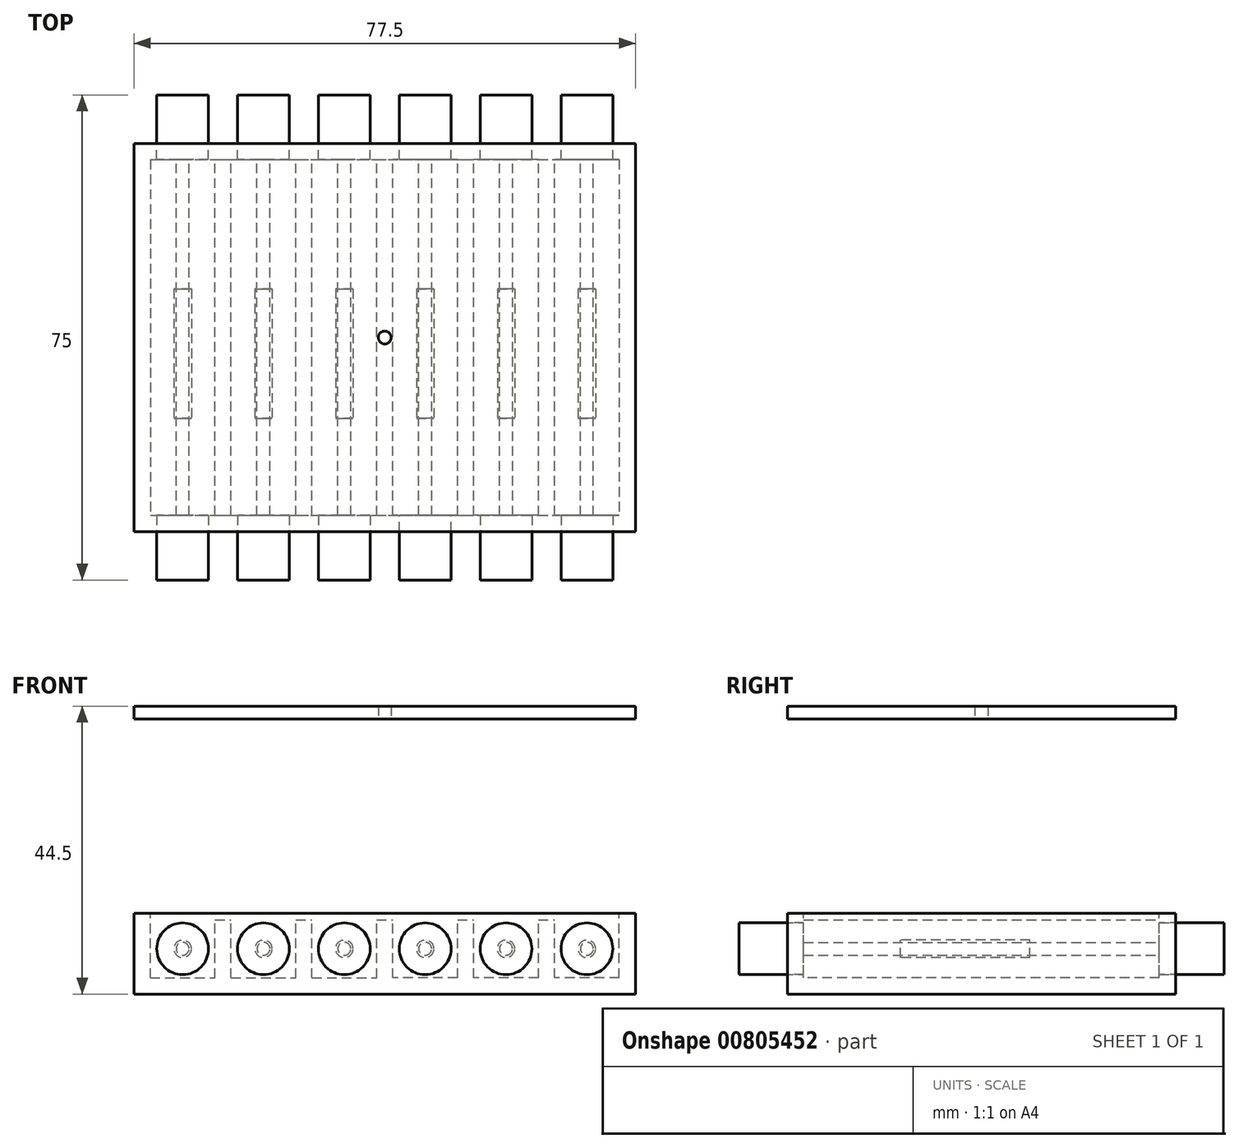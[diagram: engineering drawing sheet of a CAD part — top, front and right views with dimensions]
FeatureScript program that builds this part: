
annotation { "Feature Type Name" : "Feature", "Feature Type Description" : "" }
export const myFeature = defineFeature(function(context is Context, id is Id, definition is map)
    precondition{}
    {
        {
            var Q0;
            Q0=qCreatedBy(makeId("Top.planeOp"),FACE);
            var sketch = newSketch(context, id + "F0", { "sketchPlane" : qUnion([Q0])});
            skLineSegment(sketch, "E0.bottom", {"start": v(38.75, -30) * mm, "end": v(-38.75, -30) * mm});
            skLineSegment(sketch, "E0.top", {"start": v(38.75, 30) * mm, "end": v(-38.75, 30) * mm});
            skLineSegment(sketch, "E0.left", {"start": v(38.75, -30) * mm, "end": v(38.75, 30) * mm});
            skLineSegment(sketch, "E0.right", {"start": v(-38.75, -30) * mm, "end": v(-38.75, 30) * mm});
            skPoint(sketch, "E0.middle", {"position": v(0, 0) * mm});
            skSolve(sketch);
        }
        {
            var Q0;
            Q0 = qSketchRegion(id + "F0", true);
            extrude(context, id + "F1", {"entities" : qUnion([Q0]), "depth" : 12.5 * mm, "offsetDistance" : 25 * mm});
        }
        {
            var Q0;
            Q0=makeQuery(id+"F1.opExtrude","CAP_FACE",FACE,{"disambiguationData":[OSD([sQuery(id+"F0.wireOp",EDGE,"E0.bottom"),sQuery(id+"F0.wireOp",EDGE,"E0.top"),sQuery(id+"F0.wireOp",EDGE,"E0.left"),sQuery(id+"F0.wireOp",EDGE,"E0.right")])],"isStart":false});
            var sketch = newSketch(context, id + "F2", { "sketchPlane" : qUnion([Q0])});
            skLineSegment(sketch, "E1.bottom", {"start": v(-36.25, 27.5) * mm, "end": v(-26.25, 27.5) * mm});
            skLineSegment(sketch, "E1.top", {"start": v(-36.25, -27.5) * mm, "end": v(-26.25, -27.5) * mm});
            skLineSegment(sketch, "E1.left", {"start": v(-36.25, 27.5) * mm, "end": v(-36.25, -27.5) * mm});
            skLineSegment(sketch, "E1.right", {"start": v(-26.25, 27.5) * mm, "end": v(-26.25, -27.5) * mm});
            skLineSegment(sketch, "E2.MirrorCS", {"start": v(36.25, 27.5) * mm, "end": v(26.25, 27.5) * mm});
            skLineSegment(sketch, "E3.MirrorCS", {"start": v(36.25, 27.5) * mm, "end": v(36.25, -27.5) * mm});
            skLineSegment(sketch, "E4.MirrorCS", {"start": v(26.25, 27.5) * mm, "end": v(26.25, -27.5) * mm});
            skLineSegment(sketch, "E5.MirrorCS", {"start": v(36.25, -27.5) * mm, "end": v(26.25, -27.5) * mm});
            skLineSegment(sketch, "E6.bottom", {"start": v(-23.75, 27.5) * mm, "end": v(-13.75, 27.5) * mm});
            skLineSegment(sketch, "E6.top", {"start": v(-23.75, -27.5) * mm, "end": v(-13.75, -27.5) * mm});
            skLineSegment(sketch, "E6.left", {"start": v(-23.75, 27.5) * mm, "end": v(-23.75, -27.5) * mm});
            skLineSegment(sketch, "E6.right", {"start": v(-13.75, 27.5) * mm, "end": v(-13.75, -27.5) * mm});
            skPoint(sketch, "E7.firstSnap0", {"position": v(-18.75, 27.5) * mm});
            skLineSegment(sketch, "E7.bottom", {"start": v(-11.25, 27.5) * mm, "end": v(-1.25, 27.5) * mm});
            skLineSegment(sketch, "E7.top", {"start": v(-11.25, -27.5) * mm, "end": v(-1.25, -27.5) * mm});
            skLineSegment(sketch, "E7.left", {"start": v(-11.25, 27.5) * mm, "end": v(-11.25, -27.5) * mm});
            skLineSegment(sketch, "E7.right", {"start": v(-1.25, 27.5) * mm, "end": v(-1.25, -27.5) * mm});
            skLineSegment(sketch, "E8.MirrorCS", {"start": v(23.75, 27.5) * mm, "end": v(13.75, 27.5) * mm});
            skLineSegment(sketch, "E9.MirrorCS", {"start": v(11.25, 27.5) * mm, "end": v(1.25, 27.5) * mm});
            skLineSegment(sketch, "E10.MirrorCS", {"start": v(13.75, 27.5) * mm, "end": v(13.75, -27.5) * mm});
            skLineSegment(sketch, "E11.MirrorCS", {"start": v(11.25, 27.5) * mm, "end": v(11.25, -27.5) * mm});
            skLineSegment(sketch, "E12.MirrorCS", {"start": v(1.25, 27.5) * mm, "end": v(1.25, -27.5) * mm});
            skLineSegment(sketch, "E13.MirrorCS", {"start": v(23.75, 27.5) * mm, "end": v(23.75, -27.5) * mm});
            skLineSegment(sketch, "E14.MirrorCS", {"start": v(23.75, -27.5) * mm, "end": v(13.75, -27.5) * mm});
            skLineSegment(sketch, "E15.MirrorCS", {"start": v(11.25, -27.5) * mm, "end": v(1.25, -27.5) * mm});
            skSolve(sketch);
        }
        {
            var Q0;
            Q0 = qSketchRegion(id + "F2", true);
            extrude(context, id + "F3", {"entities" : qUnion([Q0]), "operationType" : NewBodyOperationType.REMOVE, "oppositeDirection" : true, "depth" : 10 * mm, "offsetDistance" : 25 * mm});
        }
        {
            var Q0;
            Q0=makeQuery(id+"F1.opExtrude","SWEPT_FACE",FACE,{"disambiguationData":[OSD([sQuery(id+"F0.wireOp",EDGE,"E0.bottom")])]});
            var sketch = newSketch(context, id + "F4", { "sketchPlane" : qUnion([Q0])});
            skCircle(sketch, "E16", {"center": v(-31.25, 7) * mm, "radius": 4 * mm});
            skCircle(sketch, "E17", {"center": v(-18.75, 7) * mm, "radius": 4 * mm});
            skCircle(sketch, "E18", {"center": v(-6.25, 7) * mm, "radius": 4 * mm});
            skCircle(sketch, "E19.MirrorC", {"center": v(6.25, 7) * mm, "radius": 4 * mm});
            skCircle(sketch, "E20.MirrorC", {"center": v(18.75, 7) * mm, "radius": 4 * mm});
            skCircle(sketch, "E21.MirrorC", {"center": v(31.25, 7) * mm, "radius": 4 * mm});
            skSolve(sketch);
        }
        {
            var Q0;
            Q0 = qSketchRegion(id + "F4", true);
            var Q1;
            Q1=makeQuery(id+"F3.boolean.opBoolean","COPY",FACE,{"derivedFrom":makeQuery(id+"F3.opExtrude","SWEPT_FACE",FACE,{"disambiguationData":[OSD([sQuery(id+"F2.wireOp",EDGE,"E1.top")])]})});
            extrude(context, id + "F5", {"entities" : qUnion([Q0]), "endBound" : BoundingType.UP_TO_SURFACE, "oppositeDirection" : true, "depth" : 25 * mm, "endBoundEntityFace" : qUnion([Q1]), "offsetDistance" : 25 * mm});
        }
        {
            var Q0;
            Q0=makeQuery(id+"F1.opExtrude","CAP_FACE",FACE,{"disambiguationData":[OSD([sQuery(id+"F0.wireOp",EDGE,"E0.bottom"),sQuery(id+"F0.wireOp",EDGE,"E0.top"),sQuery(id+"F0.wireOp",EDGE,"E0.left"),sQuery(id+"F0.wireOp",EDGE,"E0.right")])],"isStart":false});
            var sketch = newSketch(context, id + "F6", { "sketchPlane" : qUnion([Q0])});
            skLineSegment(sketch, "E22.bottom", {"start": v(36.25, -27.5) * mm, "end": v(-36.25, -27.5) * mm});
            skLineSegment(sketch, "E22.top", {"start": v(36.25, 27.5) * mm, "end": v(-36.25, 27.5) * mm});
            skLineSegment(sketch, "E22.left", {"start": v(36.25, -27.5) * mm, "end": v(36.25, 27.5) * mm});
            skLineSegment(sketch, "E22.right", {"start": v(-36.25, -27.5) * mm, "end": v(-36.25, 27.5) * mm});
            skPoint(sketch, "E22.middle", {"position": v(0, 0) * mm});
            skSolve(sketch);
        }
        {
            var Q0;
            Q0 = qSketchRegion(id + "F6", true);
            extrude(context, id + "F7", {"entities" : qUnion([Q0]), "operationType" : NewBodyOperationType.REMOVE, "oppositeDirection" : true, "depth" : 1 * mm, "offsetDistance" : 25 * mm});
        }
        {
            var Q0;
            Q0=makeQuery(id+"F5.opExtrude","SWEPT_BODY",BODY,{"disambiguationData":[OSD([sQuery(id+"F4.wireOp",EDGE,"E16")])]});
            var Q1;
            Q1=makeQuery(id+"F5.opExtrude","SWEPT_BODY",BODY,{"disambiguationData":[OSD([sQuery(id+"F4.wireOp",EDGE,"E17")])]});
            var Q2;
            Q2=makeQuery(id+"F5.opExtrude","SWEPT_BODY",BODY,{"disambiguationData":[OSD([sQuery(id+"F4.wireOp",EDGE,"E18")])]});
            var Q3;
            Q3=makeQuery(id+"F5.opExtrude","SWEPT_BODY",BODY,{"disambiguationData":[OSD([sQuery(id+"F4.wireOp",EDGE,"E20.MirrorC")])]});
            var Q4;
            Q4=makeQuery(id+"F5.opExtrude","SWEPT_BODY",BODY,{"disambiguationData":[OSD([sQuery(id+"F4.wireOp",EDGE,"E21.MirrorC")])]});
            var Q5;
            Q5=makeQuery(id+"F5.opExtrude","SWEPT_BODY",BODY,{"disambiguationData":[OSD([sQuery(id+"F4.wireOp",EDGE,"E19.MirrorC")])]});
            var Q6;
            Q6=qCreatedBy(makeId("Front.planeOp"),FACE);
            mirror(context, id + "F8", {"entities" : qUnion([Q0, Q1, Q2, Q3, Q4, Q5]), "mirrorPlane" : qUnion([Q6])});
        }
        {
            var Q0;
            Q0=makeQuery(id+"F5.opExtrude","SWEPT_BODY",BODY,{"disambiguationData":[OSD([sQuery(id+"F4.wireOp",EDGE,"E16")])]});
            var Q1;
            Q1=makeQuery(id+"F8.opPattern","COPY",BODY,{"derivedFrom":makeQuery(id+"F5.opExtrude","SWEPT_BODY",BODY,{"disambiguationData":[OSD([sQuery(id+"F4.wireOp",EDGE,"E16")])]}),"instanceName":"1"});
            var Q2;
            Q2=makeQuery(id+"F5.opExtrude","SWEPT_BODY",BODY,{"disambiguationData":[OSD([sQuery(id+"F4.wireOp",EDGE,"E17")])]});
            var Q3;
            Q3=makeQuery(id+"F5.opExtrude","SWEPT_BODY",BODY,{"disambiguationData":[OSD([sQuery(id+"F4.wireOp",EDGE,"E18")])]});
            var Q4;
            Q4=makeQuery(id+"F5.opExtrude","SWEPT_BODY",BODY,{"disambiguationData":[OSD([sQuery(id+"F4.wireOp",EDGE,"E19.MirrorC")])]});
            var Q5;
            Q5=makeQuery(id+"F5.opExtrude","SWEPT_BODY",BODY,{"disambiguationData":[OSD([sQuery(id+"F4.wireOp",EDGE,"E20.MirrorC")])]});
            var Q6;
            Q6=makeQuery(id+"F5.opExtrude","SWEPT_BODY",BODY,{"disambiguationData":[OSD([sQuery(id+"F4.wireOp",EDGE,"E21.MirrorC")])]});
            var Q7;
            Q7=makeQuery(id+"F8.opPattern","COPY",BODY,{"derivedFrom":makeQuery(id+"F5.opExtrude","SWEPT_BODY",BODY,{"disambiguationData":[OSD([sQuery(id+"F4.wireOp",EDGE,"E17")])]}),"instanceName":"1"});
            var Q8;
            Q8=makeQuery(id+"F8.opPattern","COPY",BODY,{"derivedFrom":makeQuery(id+"F5.opExtrude","SWEPT_BODY",BODY,{"disambiguationData":[OSD([sQuery(id+"F4.wireOp",EDGE,"E18")])]}),"instanceName":"1"});
            var Q9;
            Q9=makeQuery(id+"F8.opPattern","COPY",BODY,{"derivedFrom":makeQuery(id+"F5.opExtrude","SWEPT_BODY",BODY,{"disambiguationData":[OSD([sQuery(id+"F4.wireOp",EDGE,"E19.MirrorC")])]}),"instanceName":"1"});
            var Q10;
            Q10=makeQuery(id+"F8.opPattern","COPY",BODY,{"derivedFrom":makeQuery(id+"F5.opExtrude","SWEPT_BODY",BODY,{"disambiguationData":[OSD([sQuery(id+"F4.wireOp",EDGE,"E20.MirrorC")])]}),"instanceName":"1"});
            var Q11;
            Q11=makeQuery(id+"F8.opPattern","COPY",BODY,{"derivedFrom":makeQuery(id+"F5.opExtrude","SWEPT_BODY",BODY,{"disambiguationData":[OSD([sQuery(id+"F4.wireOp",EDGE,"E21.MirrorC")])]}),"instanceName":"1"});
            var Q12;
            Q12=makeQuery(id+"F1.opExtrude","SWEPT_BODY",BODY,{"disambiguationData":[OSD([sQuery(id+"F0.wireOp",EDGE,"E0.bottom"),sQuery(id+"F0.wireOp",EDGE,"E0.top"),sQuery(id+"F0.wireOp",EDGE,"E0.left"),sQuery(id+"F0.wireOp",EDGE,"E0.right")])]});
            booleanBodies(context, id + "F9", {"operationType" : BooleanOperationType.SUBTRACTION, "tools" : qUnion([Q0, Q1, Q2, Q3, Q4, Q5, Q6, Q7, Q8, Q9, Q10, Q11]), "targets" : qUnion([Q12])});
        }
        {
            var Q0;
            Q0=makeQuery(id+"F1.opExtrude","CAP_FACE",FACE,{"disambiguationData":[OSD([sQuery(id+"F0.wireOp",EDGE,"E0.bottom"),sQuery(id+"F0.wireOp",EDGE,"E0.top"),sQuery(id+"F0.wireOp",EDGE,"E0.left"),sQuery(id+"F0.wireOp",EDGE,"E0.right")])],"isStart":false});
            var sketch = newSketch(context, id + "F10", { "sketchPlane" : qUnion([Q0])});
            skLineSegment(sketch, "E23.bottom", {"start": v(-38.75, 30) * mm, "end": v(38.75, 30) * mm});
            skLineSegment(sketch, "E23.top", {"start": v(-38.75, -30) * mm, "end": v(38.75, -30) * mm});
            skLineSegment(sketch, "E23.left", {"start": v(-38.75, 30) * mm, "end": v(-38.75, -30) * mm});
            skLineSegment(sketch, "E23.right", {"start": v(38.75, 30) * mm, "end": v(38.75, -30) * mm});
            skPoint(sketch, "E23.middle", {"position": v(0, 0) * mm});
            skSolve(sketch);
        }
        {
            var Q0;
            Q0 = qSketchRegion(id + "F10", true);
            extrude(context, id + "F11", {"entities" : qUnion([Q0]), "depth" : 2 * mm, "offsetDistance" : 25 * mm});
        }
        {
            var Q0;
            Q0=makeQuery(id+"F11.opExtrude","SWEPT_BODY",BODY,{"disambiguationData":[OSD([sQuery(id+"F10.wireOp",EDGE,"E23.bottom"),sQuery(id+"F10.wireOp",EDGE,"E23.top"),sQuery(id+"F10.wireOp",EDGE,"E23.left"),sQuery(id+"F10.wireOp",EDGE,"E23.right")])]});
            transform(context, id + "F12", {"entities" : qUnion([Q0]), "transformType" : TransformType.TRANSLATION_3D, "dx" : 0 * mm, "dy" : 0 * mm, "dz" : 30 * mm, "makeCopy" : false});
        }
        {
            var Q0;
            Q0=sQuery(id+"F10.wireOp",VERTEX,"E23.middle");
            var Q1;
            Q1=makeQuery(id+"F11.opExtrude","SWEPT_BODY",BODY,{"disambiguationData":[OSD([sQuery(id+"F10.wireOp",EDGE,"E23.bottom"),sQuery(id+"F10.wireOp",EDGE,"E23.top"),sQuery(id+"F10.wireOp",EDGE,"E23.left"),sQuery(id+"F10.wireOp",EDGE,"E23.right")])]});
            hole(context, id + "F13", {"style" : HoleStyle.SIMPLE, "endStyle" : HoleEndStyle.THROUGH, "oppositeDirection" : true, "standardTappedOrClearance" : lookupTablePath({ "standard" : "ANSI", "engagement" : "75%", "pitch" : "48 tpi", "size" : "#3", "type" : "Tapped" }), "standardBlindInLast" : lookupTablePath({ "standard" : "ANSI", "engagement" : "75%", "pitch" : "48 tpi", "size" : "#3", "type" : "Tapped" }), "holeDiameter" : 2 * mm, "majorDiameter" : 2.5 * mm, "showTappedDepth" : true, "isTappedThrough" : true, "tappedDepth" : 12 * mm, "tapClearance" : 3, "locations" : qUnion([Q0]), "scope" : qUnion([Q1])});
        }
        {
            var Q0;
            Q0=makeQuery(id+"F7.boolean.opBoolean","MERGE",FACE,{"derivedFrom":[makeQuery(id+"F3.boolean.opBoolean","COPY",FACE,{"derivedFrom":makeQuery(id+"F3.opExtrude","SWEPT_FACE",FACE,{"disambiguationData":[OSD([sQuery(id+"F2.wireOp",EDGE,"E1.bottom")])]})}),makeQuery(id+"F3.boolean.opBoolean","COPY",FACE,{"derivedFrom":makeQuery(id+"F3.opExtrude","SWEPT_FACE",FACE,{"disambiguationData":[OSD([sQuery(id+"F2.wireOp",EDGE,"E2.MirrorCS")])]})}),makeQuery(id+"F3.boolean.opBoolean","COPY",FACE,{"derivedFrom":makeQuery(id+"F3.opExtrude","SWEPT_FACE",FACE,{"disambiguationData":[OSD([sQuery(id+"F2.wireOp",EDGE,"E6.bottom")])]})}),makeQuery(id+"F3.boolean.opBoolean","COPY",FACE,{"derivedFrom":makeQuery(id+"F3.opExtrude","SWEPT_FACE",FACE,{"disambiguationData":[OSD([sQuery(id+"F2.wireOp",EDGE,"E7.bottom")])]})}),makeQuery(id+"F3.boolean.opBoolean","COPY",FACE,{"derivedFrom":makeQuery(id+"F3.opExtrude","SWEPT_FACE",FACE,{"disambiguationData":[OSD([sQuery(id+"F2.wireOp",EDGE,"E8.MirrorCS")])]})}),makeQuery(id+"F3.boolean.opBoolean","COPY",FACE,{"derivedFrom":makeQuery(id+"F3.opExtrude","SWEPT_FACE",FACE,{"disambiguationData":[OSD([sQuery(id+"F2.wireOp",EDGE,"E9.MirrorCS")])]})}),makeQuery(id+"F7.opExtrude","SWEPT_FACE",FACE,{"disambiguationData":[OSD([sQuery(id+"F6.wireOp",EDGE,"E22.top")])]})]});
            var sketch = newSketch(context, id + "F14", { "sketchPlane" : qUnion([Q0])});
            skCircle(sketch, "E24", {"center": v(-18.75, 7) * mm, "radius": 1 * mm});
            skSolve(sketch);
        }
        {
            var Q0;
            Q0 = qSketchRegion(id + "F14", true);
            var Q1;
            Q1=makeQuery(id+"F7.boolean.opBoolean","MERGE",FACE,{"derivedFrom":[makeQuery(id+"F3.boolean.opBoolean","COPY",FACE,{"derivedFrom":makeQuery(id+"F3.opExtrude","SWEPT_FACE",FACE,{"disambiguationData":[OSD([sQuery(id+"F2.wireOp",EDGE,"E1.top")])]})}),makeQuery(id+"F3.boolean.opBoolean","COPY",FACE,{"derivedFrom":makeQuery(id+"F3.opExtrude","SWEPT_FACE",FACE,{"disambiguationData":[OSD([sQuery(id+"F2.wireOp",EDGE,"E5.MirrorCS")])]})}),makeQuery(id+"F3.boolean.opBoolean","COPY",FACE,{"derivedFrom":makeQuery(id+"F3.opExtrude","SWEPT_FACE",FACE,{"disambiguationData":[OSD([sQuery(id+"F2.wireOp",EDGE,"E6.top")])]})}),makeQuery(id+"F3.boolean.opBoolean","COPY",FACE,{"derivedFrom":makeQuery(id+"F3.opExtrude","SWEPT_FACE",FACE,{"disambiguationData":[OSD([sQuery(id+"F2.wireOp",EDGE,"E7.top")])]})}),makeQuery(id+"F3.boolean.opBoolean","COPY",FACE,{"derivedFrom":makeQuery(id+"F3.opExtrude","SWEPT_FACE",FACE,{"disambiguationData":[OSD([sQuery(id+"F2.wireOp",EDGE,"E14.MirrorCS")])]})}),makeQuery(id+"F3.boolean.opBoolean","COPY",FACE,{"derivedFrom":makeQuery(id+"F3.opExtrude","SWEPT_FACE",FACE,{"disambiguationData":[OSD([sQuery(id+"F2.wireOp",EDGE,"E15.MirrorCS")])]})}),makeQuery(id+"F7.opExtrude","SWEPT_FACE",FACE,{"disambiguationData":[OSD([sQuery(id+"F6.wireOp",EDGE,"E22.bottom")])]})]});
            extrude(context, id + "F15", {"entities" : qUnion([Q0]), "endBound" : BoundingType.UP_TO_SURFACE, "depth" : 25 * mm, "endBoundEntityFace" : qUnion([Q1]), "offsetDistance" : 25 * mm});
        }
        {
            var Q0;
            Q0=makeQuery(id+"F15.opExtrude","CAP_FACE",FACE,{"disambiguationData":[OSD([sQuery(id+"F14.wireOp",EDGE,"E24")])],"isStart":false});
            var sketch = newSketch(context, id + "F16", { "sketchPlane" : qUnion([Q0])});
            skCircle(sketch, "E25", {"center": v(-18.75, 7) * mm, "radius": 1.35 * mm});
            skSolve(sketch);
        }
        {
            var Q0;
            Q0 = qSketchRegion(id + "F16", true);
            extrude(context, id + "F17", {"entities" : qUnion([Q0]), "oppositeDirection" : true, "depth" : 20 * mm, "offsetDistance" : 25 * mm});
        }
        {
            var Q0;
            Q0=makeQuery(id+"F17.opExtrude","SWEPT_BODY",BODY,{"disambiguationData":[OSD([sQuery(id+"F16.wireOp",EDGE,"E25")])]});
            transform(context, id + "F18", {"entities" : qUnion([Q0]), "transformType" : TransformType.TRANSLATION_3D, "dx" : 0 * mm, "dy" : 15 * mm, "dz" : 0 * mm, "makeCopy" : false});
        }
        {
            var Q0;
            Q0=makeQuery(id+"F15.opExtrude","SWEPT_BODY",BODY,{"disambiguationData":[OSD([sQuery(id+"F14.wireOp",EDGE,"E24")])]});
            var Q1;
            Q1=makeQuery(id+"F17.opExtrude","SWEPT_BODY",BODY,{"disambiguationData":[OSD([sQuery(id+"F16.wireOp",EDGE,"E25")])]});
            transform(context, id + "F19", {"entities" : qUnion([Q0, Q1]), "transformType" : TransformType.COPY});
        }
        {
            var Q0;
            Q0=makeQuery(id+"F19.opPattern","COPY",BODY,{"derivedFrom":makeQuery(id+"F17.opExtrude","SWEPT_BODY",BODY,{"disambiguationData":[OSD([sQuery(id+"F16.wireOp",EDGE,"E25")])]}),"instanceName":"1"});
            var Q1;
            Q1=makeQuery(id+"F19.opPattern","COPY",BODY,{"derivedFrom":makeQuery(id+"F15.opExtrude","SWEPT_BODY",BODY,{"disambiguationData":[OSD([sQuery(id+"F14.wireOp",EDGE,"E24")])]}),"instanceName":"1"});
            transform(context, id + "F20", {"entities" : qUnion([Q0, Q1]), "transformType" : TransformType.TRANSLATION_3D, "dx" : 12.5 * mm, "dy" : 0 * mm, "dz" : 0 * mm, "makeCopy" : false});
        }
        {
            var Q0;
            Q0=makeQuery(id+"F15.opExtrude","SWEPT_BODY",BODY,{"disambiguationData":[OSD([sQuery(id+"F14.wireOp",EDGE,"E24")])]});
            var Q1;
            Q1=makeQuery(id+"F17.opExtrude","SWEPT_BODY",BODY,{"disambiguationData":[OSD([sQuery(id+"F16.wireOp",EDGE,"E25")])]});
            transform(context, id + "F21", {"entities" : qUnion([Q0, Q1]), "transformType" : TransformType.COPY});
        }
        {
            var Q0;
            Q0=makeQuery(id+"F21.opPattern","COPY",BODY,{"derivedFrom":makeQuery(id+"F17.opExtrude","SWEPT_BODY",BODY,{"disambiguationData":[OSD([sQuery(id+"F16.wireOp",EDGE,"E25")])]}),"instanceName":"1"});
            var Q1;
            Q1=makeQuery(id+"F21.opPattern","COPY",BODY,{"derivedFrom":makeQuery(id+"F15.opExtrude","SWEPT_BODY",BODY,{"disambiguationData":[OSD([sQuery(id+"F14.wireOp",EDGE,"E24")])]}),"instanceName":"1"});
            transform(context, id + "F22", {"entities" : qUnion([Q0, Q1]), "transformType" : TransformType.TRANSLATION_3D, "dx" : -12.5 * mm, "dy" : 0 * mm, "dz" : 0 * mm, "makeCopy" : false});
        }
        {
            var Q0;
            Q0=makeQuery(id+"F15.opExtrude","SWEPT_BODY",BODY,{"disambiguationData":[OSD([sQuery(id+"F14.wireOp",EDGE,"E24")])]});
            var Q1;
            Q1=makeQuery(id+"F17.opExtrude","SWEPT_BODY",BODY,{"disambiguationData":[OSD([sQuery(id+"F16.wireOp",EDGE,"E25")])]});
            var Q2;
            Q2=makeQuery(id+"F21.opPattern","COPY",BODY,{"derivedFrom":makeQuery(id+"F15.opExtrude","SWEPT_BODY",BODY,{"disambiguationData":[OSD([sQuery(id+"F14.wireOp",EDGE,"E24")])]}),"instanceName":"1"});
            var Q3;
            Q3=makeQuery(id+"F21.opPattern","COPY",BODY,{"derivedFrom":makeQuery(id+"F17.opExtrude","SWEPT_BODY",BODY,{"disambiguationData":[OSD([sQuery(id+"F16.wireOp",EDGE,"E25")])]}),"instanceName":"1"});
            var Q4;
            Q4=makeQuery(id+"F19.opPattern","COPY",BODY,{"derivedFrom":makeQuery(id+"F15.opExtrude","SWEPT_BODY",BODY,{"disambiguationData":[OSD([sQuery(id+"F14.wireOp",EDGE,"E24")])]}),"instanceName":"1"});
            var Q5;
            Q5=makeQuery(id+"F19.opPattern","COPY",BODY,{"derivedFrom":makeQuery(id+"F17.opExtrude","SWEPT_BODY",BODY,{"disambiguationData":[OSD([sQuery(id+"F16.wireOp",EDGE,"E25")])]}),"instanceName":"1"});
            var Q6;
            Q6=qCreatedBy(makeId("Right.planeOp"),FACE);
            mirror(context, id + "F23", {"entities" : qUnion([Q0, Q1, Q2, Q3, Q4, Q5]), "mirrorPlane" : qUnion([Q6])});
        }
        {
            var Q0;
            Q0=makeQuery(id+"F1.opExtrude","SWEPT_FACE",FACE,{"disambiguationData":[OSD([sQuery(id+"F0.wireOp",EDGE,"E0.top")])]});
            var sketch = newSketch(context, id + "F24", { "sketchPlane" : qUnion([Q0])});
            skCircle(sketch, "E26", {"center": v(-31.25, 7) * mm, "radius": 4 * mm});
            skSolve(sketch);
        }
        {
            var Q0;
            Q0 = qSketchRegion(id + "F24", true);
            extrude(context, id + "F25", {"entities" : qUnion([Q0]), "depth" : 10 * mm, "offsetDistance" : 25 * mm});
        }
        {
            var Q0;
            Q0=makeQuery(id+"F25.opExtrude","SWEPT_BODY",BODY,{"disambiguationData":[OSD([sQuery(id+"F24.wireOp",EDGE,"E26")])]});
            transform(context, id + "F26", {"entities" : qUnion([Q0]), "transformType" : TransformType.TRANSLATION_3D, "dx" : 0 * mm, "dy" : -2.5 * mm, "dz" : 0 * mm, "makeCopy" : false});
        }
        {
            var Q0;
            Q0=makeQuery(id+"F25.opExtrude","SWEPT_BODY",BODY,{"disambiguationData":[OSD([sQuery(id+"F24.wireOp",EDGE,"E26")])]});
            var Q1;
            Q1=qCreatedBy(makeId("Front.planeOp"),FACE);
            mirror(context, id + "F27", {"entities" : qUnion([Q0]), "mirrorPlane" : qUnion([Q1])});
        }
        {
            var Q0;
            Q0=makeQuery(id+"F25.opExtrude","SWEPT_BODY",BODY,{"disambiguationData":[OSD([sQuery(id+"F24.wireOp",EDGE,"E26")])]});
            var Q1;
            Q1=makeQuery(id+"F27.opPattern","COPY",BODY,{"derivedFrom":makeQuery(id+"F25.opExtrude","SWEPT_BODY",BODY,{"disambiguationData":[OSD([sQuery(id+"F24.wireOp",EDGE,"E26")])]}),"instanceName":"1"});
            var Q2;
            Q2=qCreatedBy(makeId("Right.planeOp"),FACE);
            mirror(context, id + "F28", {"entities" : qUnion([Q0, Q1]), "mirrorPlane" : qUnion([Q2])});
        }
        {
            var Q0;
            Q0=makeQuery(id+"F28.opPattern","COPY",BODY,{"derivedFrom":makeQuery(id+"F25.opExtrude","SWEPT_BODY",BODY,{"disambiguationData":[OSD([sQuery(id+"F24.wireOp",EDGE,"E26")])]}),"instanceName":"1"});
            var Q1;
            Q1=makeQuery(id+"F28.opPattern","COPY",BODY,{"derivedFrom":makeQuery(id+"F27.opPattern","COPY",BODY,{"derivedFrom":makeQuery(id+"F25.opExtrude","SWEPT_BODY",BODY,{"disambiguationData":[OSD([sQuery(id+"F24.wireOp",EDGE,"E26")])]}),"instanceName":"1"}),"instanceName":"1"});
            transform(context, id + "F29", {"entities" : qUnion([Q0, Q1]), "transformType" : TransformType.TRANSLATION_3D, "dx" : 12.5 * mm, "dy" : 0 * mm, "dz" : 0 * mm, "makeCopy" : true});
        }
        {
            var Q0;
            Q0=makeQuery(id+"F29.opPattern","COPY",BODY,{"derivedFrom":makeQuery(id+"F28.opPattern","COPY",BODY,{"derivedFrom":makeQuery(id+"F25.opExtrude","SWEPT_BODY",BODY,{"disambiguationData":[OSD([sQuery(id+"F24.wireOp",EDGE,"E26")])]}),"instanceName":"1"}),"instanceName":"1"});
            var Q1;
            Q1=makeQuery(id+"F29.opPattern","COPY",BODY,{"derivedFrom":makeQuery(id+"F28.opPattern","COPY",BODY,{"derivedFrom":makeQuery(id+"F27.opPattern","COPY",BODY,{"derivedFrom":makeQuery(id+"F25.opExtrude","SWEPT_BODY",BODY,{"disambiguationData":[OSD([sQuery(id+"F24.wireOp",EDGE,"E26")])]}),"instanceName":"1"}),"instanceName":"1"}),"instanceName":"1"});
            transform(context, id + "F30", {"entities" : qUnion([Q0, Q1]), "transformType" : TransformType.TRANSLATION_3D, "dx" : 12.5 * mm, "dy" : 0 * mm, "dz" : 0 * mm, "makeCopy" : true});
        }
        {
            var Q0;
            Q0=makeQuery(id+"F30.opPattern","COPY",BODY,{"derivedFrom":makeQuery(id+"F29.opPattern","COPY",BODY,{"derivedFrom":makeQuery(id+"F28.opPattern","COPY",BODY,{"derivedFrom":makeQuery(id+"F27.opPattern","COPY",BODY,{"derivedFrom":makeQuery(id+"F25.opExtrude","SWEPT_BODY",BODY,{"disambiguationData":[OSD([sQuery(id+"F24.wireOp",EDGE,"E26")])]}),"instanceName":"1"}),"instanceName":"1"}),"instanceName":"1"}),"instanceName":"1"});
            var Q1;
            Q1=makeQuery(id+"F30.opPattern","COPY",BODY,{"derivedFrom":makeQuery(id+"F29.opPattern","COPY",BODY,{"derivedFrom":makeQuery(id+"F28.opPattern","COPY",BODY,{"derivedFrom":makeQuery(id+"F25.opExtrude","SWEPT_BODY",BODY,{"disambiguationData":[OSD([sQuery(id+"F24.wireOp",EDGE,"E26")])]}),"instanceName":"1"}),"instanceName":"1"}),"instanceName":"1"});
            var Q2;
            Q2=makeQuery(id+"F29.opPattern","COPY",BODY,{"derivedFrom":makeQuery(id+"F28.opPattern","COPY",BODY,{"derivedFrom":makeQuery(id+"F25.opExtrude","SWEPT_BODY",BODY,{"disambiguationData":[OSD([sQuery(id+"F24.wireOp",EDGE,"E26")])]}),"instanceName":"1"}),"instanceName":"1"});
            var Q3;
            Q3=makeQuery(id+"F29.opPattern","COPY",BODY,{"derivedFrom":makeQuery(id+"F28.opPattern","COPY",BODY,{"derivedFrom":makeQuery(id+"F27.opPattern","COPY",BODY,{"derivedFrom":makeQuery(id+"F25.opExtrude","SWEPT_BODY",BODY,{"disambiguationData":[OSD([sQuery(id+"F24.wireOp",EDGE,"E26")])]}),"instanceName":"1"}),"instanceName":"1"}),"instanceName":"1"});
            var Q4;
            Q4=qCreatedBy(makeId("Right.planeOp"),FACE);
            mirror(context, id + "F31", {"entities" : qUnion([Q0, Q1, Q2, Q3]), "mirrorPlane" : qUnion([Q4])});
        }
    });
